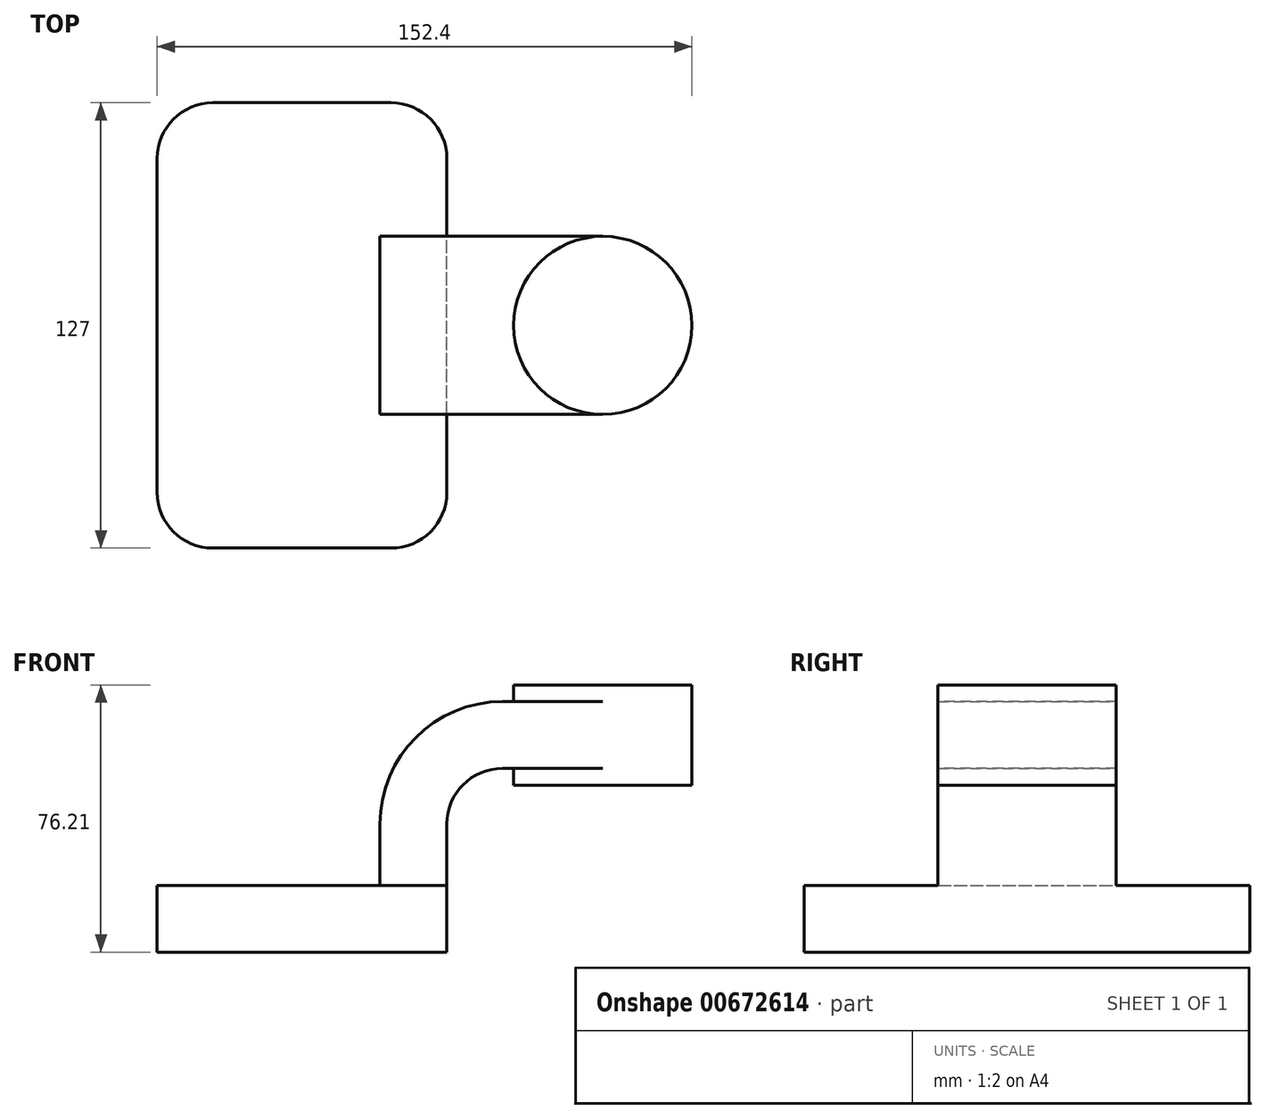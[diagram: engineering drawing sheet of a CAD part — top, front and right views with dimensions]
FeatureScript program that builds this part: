
annotation { "Feature Type Name" : "Feature", "Feature Type Description" : "" }
export const myFeature = defineFeature(function(context is Context, id is Id, definition is map)
    precondition{}
    {
        {
            var Q0;
            Q0=qCreatedBy(makeId("Front.planeOp"),FACE);
            var sketch = newSketch(context, id + "F0", { "sketchPlane" : qUnion([Q0])});
            skLineSegment(sketch, "E0.bottom", {"start": v(0, 0) * mm, "end": v(82.55, 0) * mm});
            skLineSegment(sketch, "E0.top", {"start": v(0, 19.05) * mm, "end": v(82.55, 19.05) * mm});
            skLineSegment(sketch, "E0.left", {"start": v(0, 0) * mm, "end": v(0, 19.05) * mm});
            skLineSegment(sketch, "E0.right", {"start": v(82.55, 0) * mm, "end": v(82.55, 19.05) * mm});
            skLineSegment(sketch, "E1.bottom", {"start": v(101.6, 76.21) * mm, "end": v(152.4, 76.21) * mm});
            skLineSegment(sketch, "E1.top", {"start": v(101.6, 47.64) * mm, "end": v(152.4, 47.64) * mm});
            skLineSegment(sketch, "E1.left", {"start": v(101.6, 76.21) * mm, "end": v(101.6, 47.64) * mm});
            skLineSegment(sketch, "E1.right", {"start": v(152.4, 76.21) * mm, "end": v(152.4, 47.64) * mm});
            skLineSegment(sketch, "E2", {"start": v(82.55, 19.05) * mm, "end": v(82.55, 36.53) * mm});
            skArc(sketch, "E3", {"start": v(82.55, 36.53) * mm, "mid": v(87.2, 47.75) * mm, "end": v(98.43, 52.4) * mm});
            skLineSegment(sketch, "E4", {"start": v(98.43, 52.4) * mm, "end": v(127, 52.4) * mm});
            skLineSegment(sketch, "E5", {"start": v(127, 76.21) * mm, "end": v(127, 47.64) * mm});
            skLineSegment(sketch, "E6.0", {"start": v(98.43, 71.45) * mm, "end": v(127, 71.45) * mm});
            skArc(sketch, "E6.1", {"start": v(63.5, 36.53) * mm, "mid": v(73.73, 61.22) * mm, "end": v(98.43, 71.45) * mm});
            skLineSegment(sketch, "E6.2", {"start": v(63.5, 19.05) * mm, "end": v(63.5, 36.53) * mm});
            skFitSpline(sketch, "E7", {"points": [v(98.43, 71.45) * mm, v(0, 19.05) * mm], "startDerivative": vector(-125.94, 0) * mm, "endDerivative": vector(-30.78, -115.71) * mm});
            skPoint(sketch, "E8", {"position": v(127, 61.93) * mm});
            skSolve(sketch);
        }
        {
            var Q0;
            Q0=makeQuery(id+"F0.imprint","IMPRINT",FACE,{"disambiguationData":[TD([[makeQuery(id+"F0.imprint","IMPRINT",EDGE,{"derivedFrom":sQuery(id+"F0.wireOp",EDGE,"E0.bottom")}),1.0]])]});
            extrude(context, id + "F1", {"entities" : qUnion([Q0]), "endBound" : BoundingType.SYMMETRIC, "depth" : 127 * mm, "offsetDistance" : 25.4 * mm});
        }
        {
            var Q0;
            {var subQ1=sQuery(id+"F0.wireOp",EDGE,"E2");Q0=makeQuery(id+"F0.imprint","IMPRINT",FACE,{"disambiguationData":[TD([[makeQuery(id+"F0.imprint","IMPRINT",EDGE,{"derivedFrom":subQ1}),1.0]])]});}
            var Q1;
            {var subQ0=sQuery(id+"F0.wireOp",EDGE,"E6.0");var subQ1=sQuery(id+"F0.wireOp",EDGE,"E1.left");var subQ2=makeQuery(id+"F0.imprint","INTERSECT",VERTEX,{"derivedFrom":[subQ1,subQ0]});Q1=makeQuery(id+"F0.imprint","IMPRINT",FACE,{"disambiguationData":[TD([[makeQuery(id+"F0.imprint","IMPRINT",EDGE,{"disambiguationData":[TD([[subQ2,-1.0]])],"derivedFrom":subQ1}),1.0]])]});}
            extrude(context, id + "F2", {"entities" : qUnion([Q0, Q1]), "operationType" : NewBodyOperationType.ADD, "endBound" : BoundingType.SYMMETRIC, "depth" : 50.8 * mm, "offsetDistance" : 25.4 * mm});
        }
        {
            var Q0;
            Q0=makeQuery(id+"F0.imprint","IMPRINT",FACE,{"disambiguationData":[TD([[makeQuery(id+"F0.imprint","IMPRINT",EDGE,{"derivedFrom":sQuery(id+"F0.wireOp",EDGE,"E6.1")}),1.0]])]});
            extrude(context, id + "F3", {"entities" : qUnion([Q0]), "operationType" : NewBodyOperationType.ADD, "endBound" : BoundingType.SYMMETRIC, "depth" : 15.88 * mm, "offsetDistance" : 25.4 * mm});
        }
        {
            var Q0;
            {var subQ4=sQuery(id+"F0.wireOp",EDGE,"E1.right");Q0=makeQuery(id+"F0.imprint","IMPRINT",FACE,{"disambiguationData":[TD([[makeQuery(id+"F0.imprint","IMPRINT",EDGE,{"derivedFrom":subQ4}),-1.0]])]});}
            var Q1;
            Q1=sQuery(id+"F0.wireOp",EDGE,"E5");
            revolve(context, id + "F4", {"operationType" : NewBodyOperationType.ADD, "entities" : qUnion([Q0]), "axis" : qUnion([Q1]), "revolveType" : RevolveType.FULL});
        }
        {
            var Q0;
            Q0=makeQuery(id+"F1.opExtrude","CAP_EDGE",EDGE,{"disambiguationData":[OSD([sQuery(id+"F0.wireOp",EDGE,"E0.right")])],"isStart":false});
            var Q1;
            Q1=makeQuery(id+"F1.opExtrude","CAP_EDGE",EDGE,{"disambiguationData":[OSD([sQuery(id+"F0.wireOp",EDGE,"E0.left")])],"isStart":false});
            var Q2;
            Q2=makeQuery(id+"F1.opExtrude","CAP_EDGE",EDGE,{"disambiguationData":[OSD([sQuery(id+"F0.wireOp",EDGE,"E0.left")])],"isStart":true});
            var Q3;
            Q3=makeQuery(id+"F1.opExtrude","CAP_EDGE",EDGE,{"disambiguationData":[OSD([sQuery(id+"F0.wireOp",EDGE,"E0.right")])],"isStart":true});
            fillet(context, id + "F5", {"entities" : qUnion([Q0, Q1, Q2, Q3]), "radius" : 15.88 * mm, "tangentPropagation" : true, "allowEdgeOverflow" : false});
        }
    });
